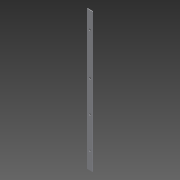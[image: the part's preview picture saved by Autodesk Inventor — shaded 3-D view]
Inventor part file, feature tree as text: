
AUTODESK INVENTOR PART (.ipt)
format: ipt  version: 2014 SP2 (Build 180246200, 246)  size: 95,232 bytes
history: native  units: mm
features: sketch x2, other x1, extrude x1, hole x1
ambient origin geometry x8: Origin, YZ Plane, XZ Plane, XY Plane, X Axis, Y Axis, Z Axis, Center Point
bodies: Body1 (feature_tree)
feature tree (5):
  other  "Bryła1"
  extrude  "Wyciągnięcie proste1"  Depth=15.9mm
  hole  "Otwór1"  [1 undecoded]
  sketch  "Szkic1"
  sketch  "Szkic2"
note: 1 required parameter value undecoded (feature->parameter linkage not recoverable at this tier; creation-order binding heuristic only, values carry confidence <= 0.55)
